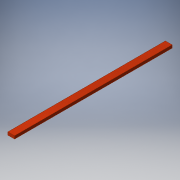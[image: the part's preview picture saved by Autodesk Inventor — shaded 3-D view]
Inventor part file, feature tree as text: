
AUTODESK INVENTOR PART (.ipt)
format: ipt  version: 2016 (Build 200138000, 138)  size: 92,160 bytes
history: native  units: in
note: dims shown in document units (in); Inventor stores cm internally (conversion verified against a paired STEP export)
features: extrude x1, sketch x1
ambient origin geometry x8: Origin, YZ Plane, XZ Plane, XY Plane, X Axis, Y Axis, Z Axis, Center Point
bodies: Solid1 (feature_tree)
feature tree (2):
  extrude  "Extrusion1"  Depth=82.0in
  sketch  "Sketch1"  dims[d0=1.5in d1=82.0in d2=3.5in d3=0.0in]
